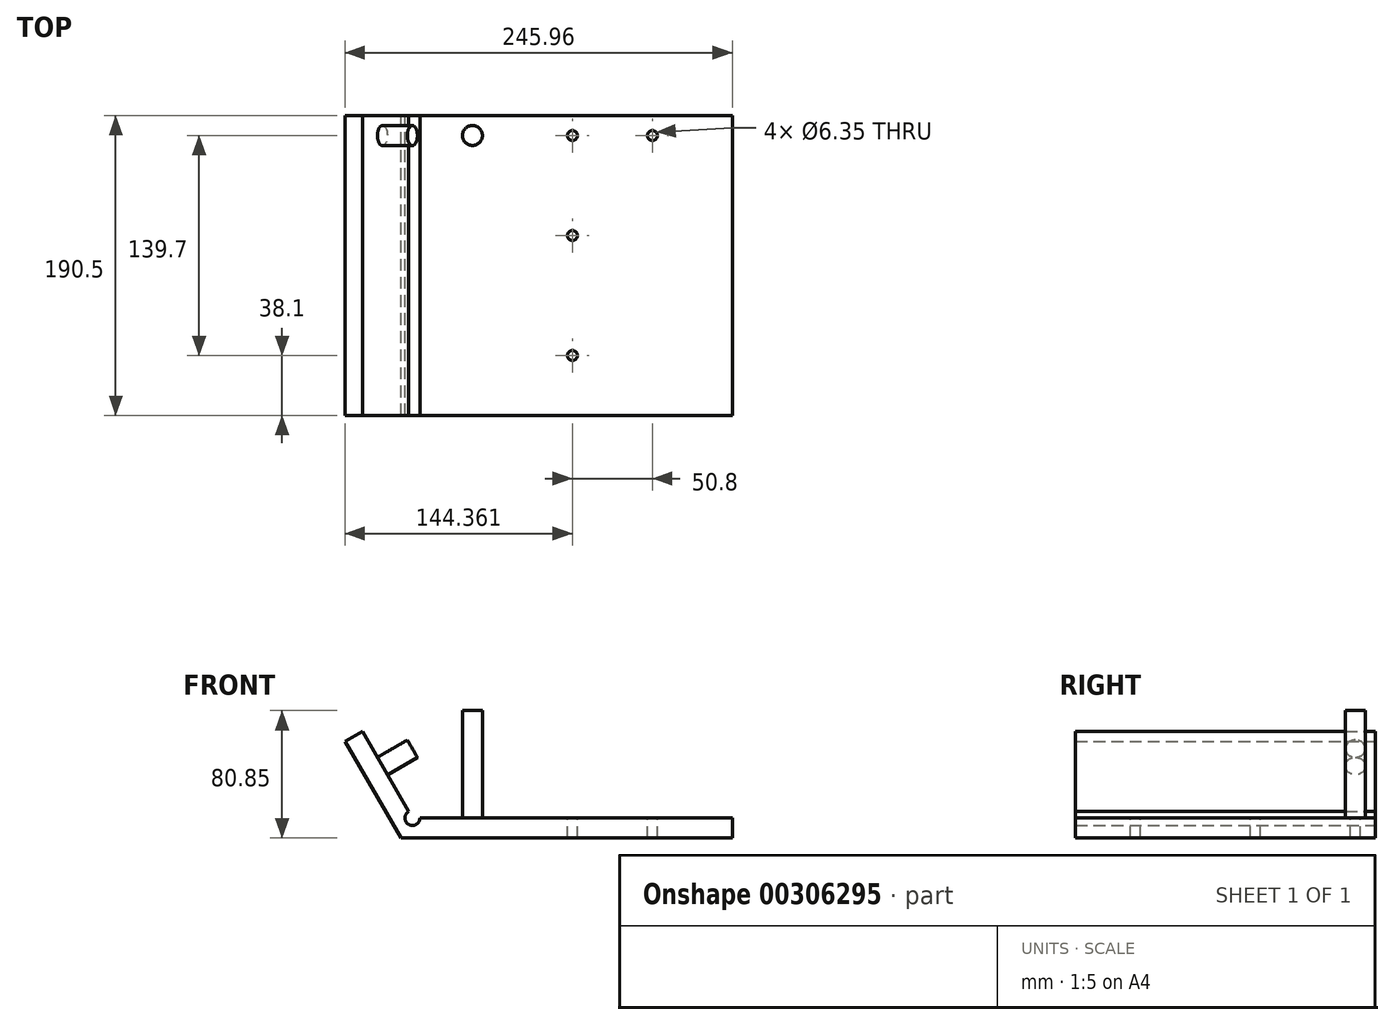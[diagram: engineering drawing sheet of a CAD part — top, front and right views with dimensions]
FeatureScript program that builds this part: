
annotation { "Feature Type Name" : "Feature", "Feature Type Description" : "" }
export const myFeature = defineFeature(function(context is Context, id is Id, definition is map)
    precondition{}
    {
        {
            var Q0;
            Q0=qCreatedBy(makeId("Front.planeOp"),FACE);
            var sketch = newSketch(context, id + "F0", { "sketchPlane" : qUnion([Q0])});
            skLineSegment(sketch, "E0", {"start": v(0, 0) * mm, "end": v(210.54, 0) * mm});
            skLineSegment(sketch, "E1", {"start": v(210.54, 0) * mm, "end": v(210.54, 12.7) * mm});
            skLineSegment(sketch, "E2", {"start": v(210.54, 12.7) * mm, "end": v(12.1, 12.7) * mm});
            skLineSegment(sketch, "E3", {"start": v(0, 0) * mm, "end": v(-35.42, 61.35) * mm});
            skLineSegment(sketch, "E4", {"start": v(0, 0) * mm, "end": v(7.34, 0) * mm});
            skPoint(sketch, "E5.start.orphan", {"position": v(0, 12.7) * mm});
            skLineSegment(sketch, "E6", {"start": v(4.96, 16.82) * mm, "end": v(-24.42, 67.7) * mm});
            skLineSegment(sketch, "E7", {"start": v(-35.42, 61.35) * mm, "end": v(-24.42, 67.7) * mm});
            skArc(sketch, "E8", {"start": v(4.96, 16.82) * mm, "mid": v(4.96, 8.58) * mm, "end": v(12.1, 12.7) * mm});
            skSolve(sketch);
        }
        {
            var Q0;
            Q0=makeQuery(id+"F0.imprint","IMPRINT",FACE,{"disambiguationData":[TD([[makeQuery(id+"F0.imprint","IMPRINT",EDGE,{"derivedFrom":sQuery(id+"F0.wireOp",EDGE,"E0")}),1.0]])]});
            extrude(context, id + "F1", {"entities" : qUnion([Q0]), "depth" : 190.5 * mm});
        }
        {
            var Q0;
            Q0=makeQuery(id+"F1.opExtrude","SWEPT_FACE",FACE,{"disambiguationData":[OSD([sQuery(id+"F0.wireOp",EDGE,"E2")])]});
            var sketch = newSketch(context, id + "F2", { "sketchPlane" : qUnion([Q0])});
            skLineSegment(sketch, "E9", {"start": v(210.54, -190.5) * mm, "end": v(108.94, -190.5) * mm});
            skLineSegment(sketch, "E10", {"start": v(210.54, -190.5) * mm, "end": v(159.74, -190.5) * mm});
            skLineSegment(sketch, "E11", {"start": v(210.54, 0) * mm, "end": v(108.94, 0) * mm});
            skLineSegment(sketch, "E12", {"start": v(210.54, -190.5) * mm, "end": v(210.54, -152.4) * mm});
            skLineSegment(sketch, "E13", {"start": v(210.54, -190.5) * mm, "end": v(210.54, -76.2) * mm});
            skLineSegment(sketch, "E14", {"start": v(210.54, -190.5) * mm, "end": v(210.54, -12.7) * mm});
            skCircle(sketch, "E15", {"center": v(108.94, -12.7) * mm, "radius": 3.18 * mm});
            skCircle(sketch, "E16", {"center": v(108.94, -76.2) * mm, "radius": 3.18 * mm});
            skCircle(sketch, "E17", {"center": v(108.94, -152.4) * mm, "radius": 3.18 * mm});
            skCircle(sketch, "E18", {"center": v(159.74, -12.7) * mm, "radius": 3.18 * mm});
            skSolve(sketch);
        }
        {
            var Q0;
            Q0=makeQuery(id+"F2.imprint","IMPRINT",FACE,{"disambiguationData":[TD([[makeQuery(id+"F2.imprint","IMPRINT",EDGE,{"derivedFrom":sQuery(id+"F2.wireOp",EDGE,"E15")}),1.0]])]});
            var Q1;
            Q1=makeQuery(id+"F2.imprint","IMPRINT",FACE,{"disambiguationData":[TD([[makeQuery(id+"F2.imprint","IMPRINT",EDGE,{"derivedFrom":sQuery(id+"F2.wireOp",EDGE,"E16")}),1.0]])]});
            var Q2;
            Q2=makeQuery(id+"F2.imprint","IMPRINT",FACE,{"disambiguationData":[TD([[makeQuery(id+"F2.imprint","IMPRINT",EDGE,{"derivedFrom":sQuery(id+"F2.wireOp",EDGE,"E18")}),1.0]])]});
            var Q3;
            Q3=makeQuery(id+"F2.imprint","IMPRINT",FACE,{"disambiguationData":[TD([[makeQuery(id+"F2.imprint","IMPRINT",EDGE,{"derivedFrom":sQuery(id+"F2.wireOp",EDGE,"E17")}),1.0]])]});
            extrude(context, id + "F3", {"entities" : qUnion([Q0, Q1, Q2, Q3]), "operationType" : NewBodyOperationType.REMOVE, "oppositeDirection" : true, "depth" : 25.4 * mm});
        }
        {
            var Q0;
            Q0=makeQuery(id+"F1.opExtrude","SWEPT_FACE",FACE,{"disambiguationData":[OSD([sQuery(id+"F0.wireOp",EDGE,"E2")])]});
            var sketch = newSketch(context, id + "F4", { "sketchPlane" : qUnion([Q0])});
            skLineSegment(sketch, "E19", {"start": v(210.54, 0) * mm, "end": v(45.44, 0) * mm});
            skLineSegment(sketch, "E20", {"start": v(45.44, 0) * mm, "end": v(45.44, -12.7) * mm});
            skLineSegment(sketch, "E21", {"start": v(108.94, -12.7) * mm, "end": v(45.44, -12.7) * mm});
            skCircle(sketch, "E22", {"center": v(45.44, -12.7) * mm, "radius": 6.35 * mm});
            skSolve(sketch);
        }
        {
            var Q0;
            Q0 = qSketchRegion(id + "F4", true);
            extrude(context, id + "F5", {"entities" : qUnion([Q0]), "operationType" : NewBodyOperationType.ADD, "depth" : 68.15 * mm});
        }
        {
            var Q0;
            Q0=makeQuery(id+"F1.opExtrude","SWEPT_FACE",FACE,{"disambiguationData":[OSD([sQuery(id+"F0.wireOp",EDGE,"E6")])]});
            var sketch = newSketch(context, id + "F6", { "sketchPlane" : qUnion([Q0])});
            skLineSegment(sketch, "E23", {"start": v(0, 70.84) * mm, "end": v(0, 45.44) * mm});
            skLineSegment(sketch, "E24", {"start": v(0, 45.44) * mm, "end": v(-12.7, 45.44) * mm});
            skCircle(sketch, "E25", {"center": v(-12.7, 45.44) * mm, "radius": 6.35 * mm});
            skSolve(sketch);
        }
        {
            var Q0;
            Q0 = qSketchRegion(id + "F6", true);
            extrude(context, id + "F7", {"entities" : qUnion([Q0]), "operationType" : NewBodyOperationType.ADD, "depth" : 22 * mm});
        }
    });
